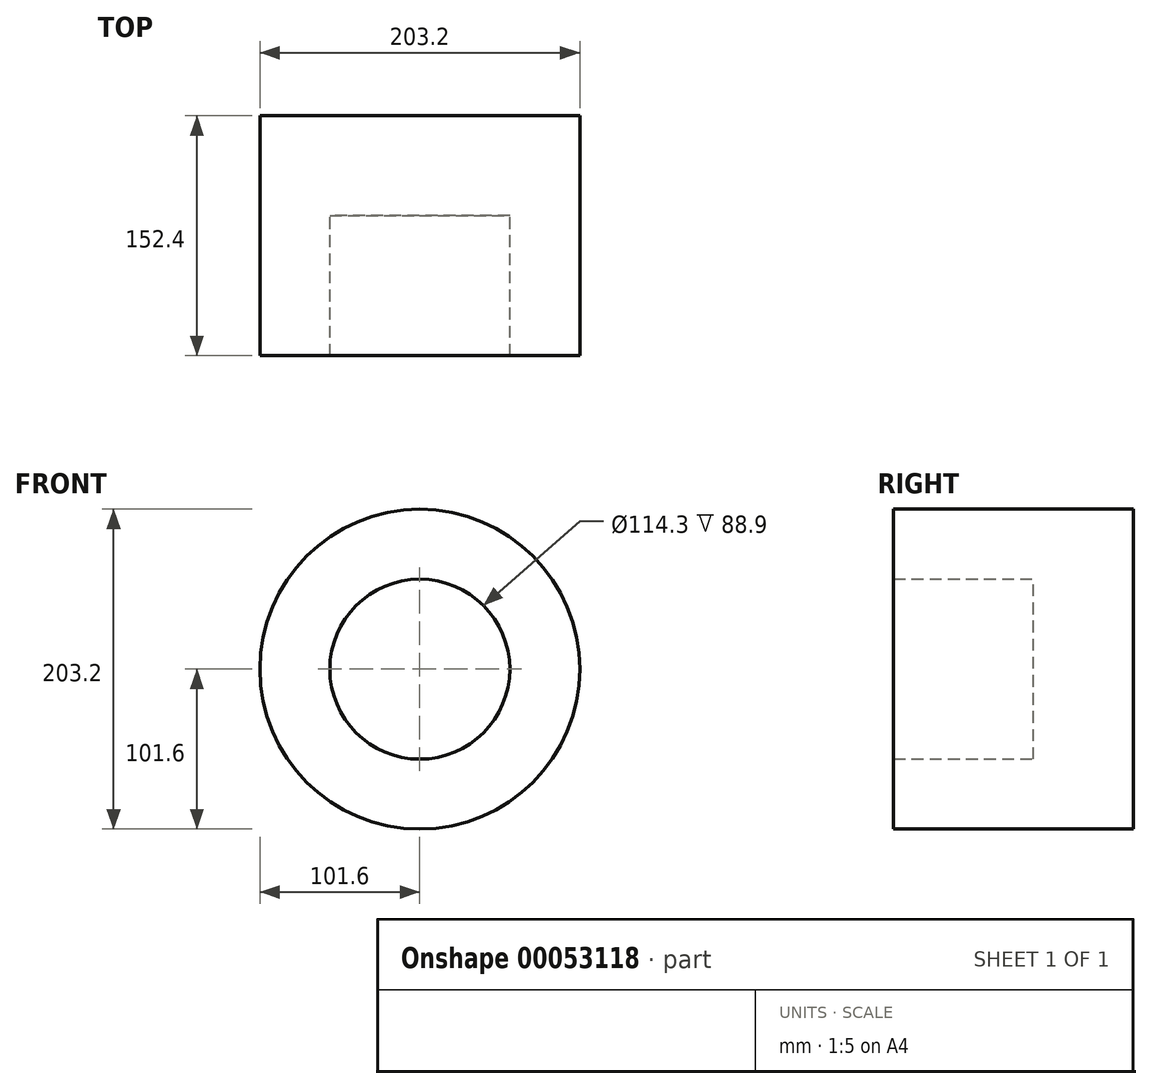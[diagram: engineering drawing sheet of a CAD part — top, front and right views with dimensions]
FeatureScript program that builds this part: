
annotation { "Feature Type Name" : "Feature", "Feature Type Description" : "" }
export const myFeature = defineFeature(function(context is Context, id is Id, definition is map)
    precondition{}
    {
        {
            var Q0;
            Q0=qCreatedBy(makeId("Front.planeOp"),FACE);
            var sketch = newSketch(context, id + "F0", { "sketchPlane" : qUnion([Q0])});
            skCircle(sketch, "E0", {"center": v(0, 0) * mm, "radius": 57.15 * mm});
            skCircle(sketch, "E1", {"center": v(0, 0) * mm, "radius": 101.6 * mm});
            skSolve(sketch);
        }
        {
            var Q0;
            Q0=makeQuery(id+"F0.imprint","IMPRINT",FACE,{"disambiguationData":[TD([[makeQuery(id+"F0.imprint","IMPRINT",EDGE,{"derivedFrom":sQuery(id+"F0.wireOp",EDGE,"E0")}),-1.0]])]});
            extrude(context, id + "F1", {"entities" : qUnion([Q0]), "depth" : 152.4 * mm});
        }
        {
            var Q0;
            Q0=qCreatedBy(makeId("Front.planeOp"),FACE);
            var sketch = newSketch(context, id + "F2", { "sketchPlane" : qUnion([Q0])});
            skCircle(sketch, "E2", {"center": v(0, 0) * mm, "radius": 57.15 * mm});
            skSolve(sketch);
        }
        {
            var Q0;
            Q0=makeQuery(id+"F2.imprint","IMPRINT",FACE,{"disambiguationData":[TD([[makeQuery(id+"F2.imprint","IMPRINT",EDGE,{"derivedFrom":sQuery(id+"F2.wireOp",EDGE,"E2")}),1.0]])]});
            extrude(context, id + "F3", {"entities" : qUnion([Q0]), "operationType" : NewBodyOperationType.ADD, "depth" : 63.5 * mm});
        }
    });
